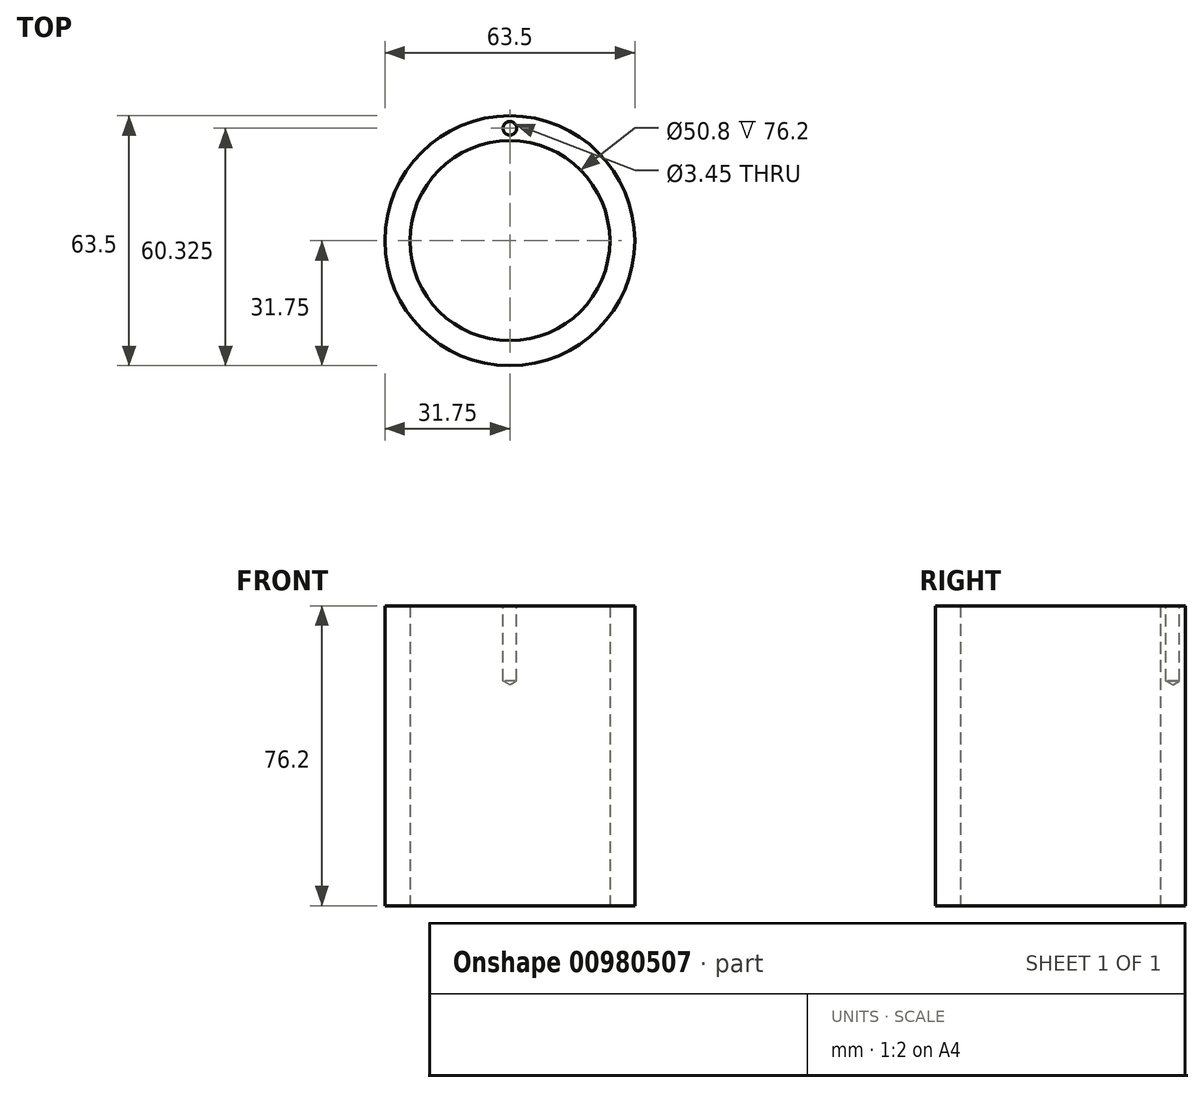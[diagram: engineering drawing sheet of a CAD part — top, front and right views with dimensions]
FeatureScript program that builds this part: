
annotation { "Feature Type Name" : "Feature", "Feature Type Description" : "" }
export const myFeature = defineFeature(function(context is Context, id is Id, definition is map)
    precondition{}
    {
        {
            var Q0;
            Q0=qCreatedBy(makeId("Top.planeOp"),FACE);
            var sketch = newSketch(context, id + "F0", { "sketchPlane" : qUnion([Q0])});
            skCircle(sketch, "E0", {"center": v(0, 0) * mm, "radius": 31.75 * mm});
            skCircle(sketch, "E1", {"center": v(0, 0) * mm, "radius": 25.4 * mm});
            skSolve(sketch);
        }
        {
            var Q0;
            Q0=makeQuery(id+"F0.imprint","IMPRINT",FACE,{"disambiguationData":[TD([[makeQuery(id+"F0.imprint","IMPRINT",EDGE,{"derivedFrom":sQuery(id+"F0.wireOp",EDGE,"E0")}),1.0]])]});
            extrude(context, id + "F1", {"entities" : qUnion([Q0]), "depth" : 76.2 * mm, "offsetDistance" : 25.4 * mm});
        }
        {
            var Q0;
            Q0=makeQuery(id+"F1.opExtrude","CAP_FACE",FACE,{"disambiguationData":[OSD([sQuery(id+"F0.wireOp",EDGE,"E0"),sQuery(id+"F0.wireOp",EDGE,"E1")])],"isStart":false});
            var sketch = newSketch(context, id + "F2", { "sketchPlane" : qUnion([Q0])});
            skPoint(sketch, "E2", {"position": v(0, 28.58) * mm});
            skLineSegment(sketch, "E3", {"start": v(0, 25.4) * mm, "end": v(0, 31.75) * mm});
            skSolve(sketch);
        }
        {
            var Q0;
            Q0=sQuery(id+"F2.wireOp",VERTEX,"E2");
            var Q1;
            Q1=makeQuery(id+"F1.opExtrude","SWEPT_BODY",BODY,{"disambiguationData":[OSD([sQuery(id+"F0.wireOp",EDGE,"E0"),sQuery(id+"F0.wireOp",EDGE,"E1")])]});
            hole(context, id + "F3", {"style" : HoleStyle.SIMPLE, "endStyle" : HoleEndStyle.BLIND, "standardTappedOrClearance" : lookupTablePath({ "standard" : "ANSI", "engagement" : "75%", "pitch" : "32 tpi", "size" : "#8", "type" : "Tapped" }), "standardBlindInLast" : lookupTablePath({ "standard" : "ANSI", "fit" : "Normal", "engagement" : "75%", "pitch" : "32 tpi", "size" : "#8", "type" : "Clearance & tapped" }), "holeDiameter" : 3.45 * mm, "majorDiameter" : 4.17 * mm, "showTappedDepth" : true, "holeDepth" : 19.05 * mm, "isTappedThrough" : true, "tappedDepth" : 16.67 * mm, "tapClearance" : 3, "startFromSketch" : true, "locations" : qUnion([Q0]), "scope" : qUnion([Q1])});
        }
    });
